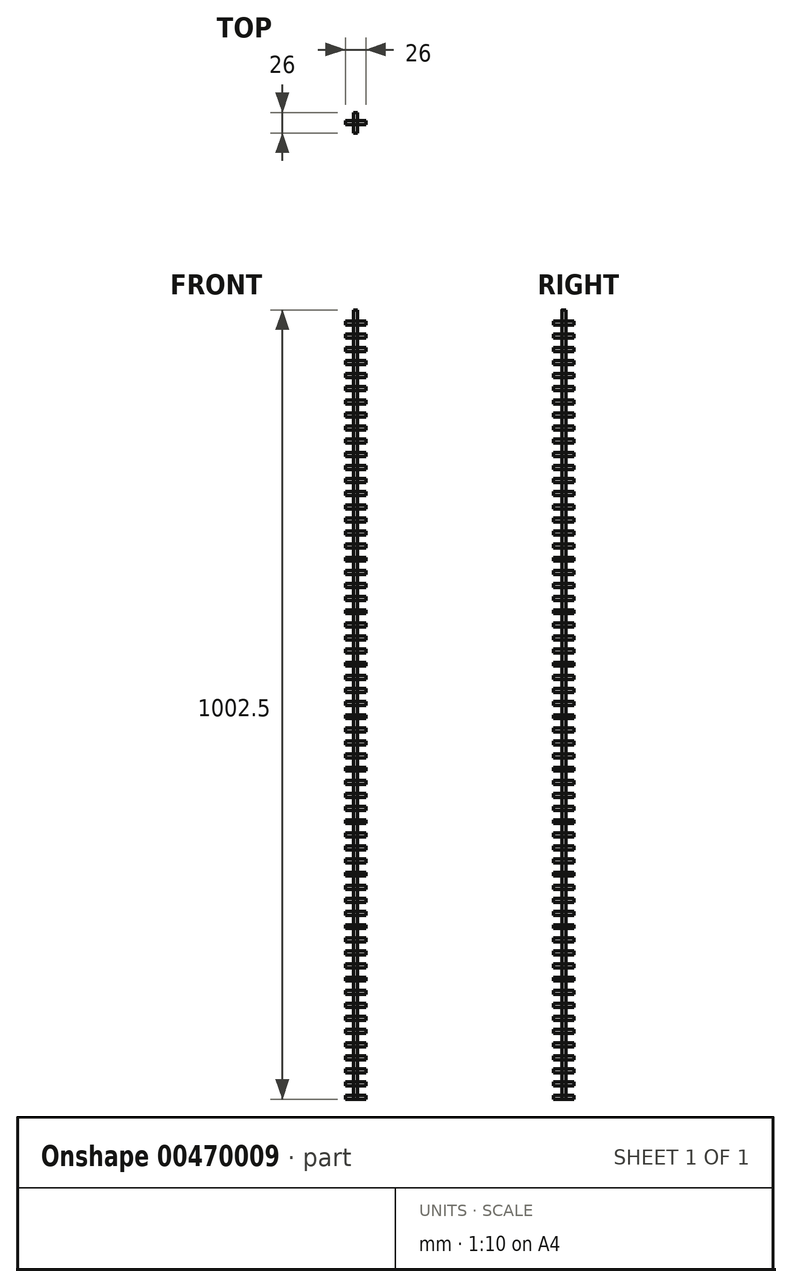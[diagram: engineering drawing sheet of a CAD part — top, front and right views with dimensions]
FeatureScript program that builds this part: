
annotation { "Feature Type Name" : "Feature", "Feature Type Description" : "" }
export const myFeature = defineFeature(function(context is Context, id is Id, definition is map)
    precondition{}
    {
        {
            var Q0;
            Q0=qCreatedBy(makeId("Top.planeOp"),FACE);
            var sketch = newSketch(context, id + "F0", { "sketchPlane" : qUnion([Q0])});
            skCircle(sketch, "E0", {"center": v(0, 0) * mm, "radius": 2.5 * mm});
            skSolve(sketch);
        }
        {
            var Q0;
            Q0 = qSketchRegion(id + "F0", true);
            extrude(context, id + "F1", {"entities" : qUnion([Q0]), "depth" : 1000 * mm, "offsetDistance" : 25 * mm});
        }
        {
            var Q0;
            Q0=qCreatedBy(makeId("Front.planeOp"),FACE);
            var sketch = newSketch(context, id + "F2", { "sketchPlane" : qUnion([Q0])});
            skLineSegment(sketch, "E1.bottom", {"start": v(2.5, 2.5) * mm, "end": v(-2.5, 2.5) * mm});
            skLineSegment(sketch, "E1.top", {"start": v(2.5, -2.5) * mm, "end": v(-2.5, -2.5) * mm});
            skLineSegment(sketch, "E1.left", {"start": v(2.5, 2.5) * mm, "end": v(2.5, -2.5) * mm});
            skLineSegment(sketch, "E1.right", {"start": v(-2.5, 2.5) * mm, "end": v(-2.5, -2.5) * mm});
            skPoint(sketch, "E1.middle", {"position": v(0, 0) * mm});
            skLineSegment(sketch, "E2.0.1.0", {"start": v(2.5, 19.17) * mm, "end": v(-2.5, 19.17) * mm});
            skLineSegment(sketch, "E2.0.1.1", {"start": v(2.5, 19.17) * mm, "end": v(2.5, 14.17) * mm});
            skLineSegment(sketch, "E2.0.1.2", {"start": v(2.5, 14.17) * mm, "end": v(-2.5, 14.17) * mm});
            skLineSegment(sketch, "E2.0.1.3", {"start": v(-2.5, 19.17) * mm, "end": v(-2.5, 14.17) * mm});
            skLineSegment(sketch, "E2.0.2.0", {"start": v(2.5, 35.83) * mm, "end": v(-2.5, 35.83) * mm});
            skLineSegment(sketch, "E2.0.2.1", {"start": v(2.5, 35.83) * mm, "end": v(2.5, 30.83) * mm});
            skLineSegment(sketch, "E2.0.2.2", {"start": v(2.5, 30.83) * mm, "end": v(-2.5, 30.83) * mm});
            skLineSegment(sketch, "E2.0.2.3", {"start": v(-2.5, 35.83) * mm, "end": v(-2.5, 30.83) * mm});
            skLineSegment(sketch, "E2.0.3.0", {"start": v(2.5, 52.5) * mm, "end": v(-2.5, 52.5) * mm});
            skLineSegment(sketch, "E2.0.3.1", {"start": v(2.5, 52.5) * mm, "end": v(2.5, 47.5) * mm});
            skLineSegment(sketch, "E2.0.3.2", {"start": v(2.5, 47.5) * mm, "end": v(-2.5, 47.5) * mm});
            skLineSegment(sketch, "E2.0.3.3", {"start": v(-2.5, 52.5) * mm, "end": v(-2.5, 47.5) * mm});
            skLineSegment(sketch, "E2.0.4.0", {"start": v(2.5, 69.17) * mm, "end": v(-2.5, 69.17) * mm});
            skLineSegment(sketch, "E2.0.4.1", {"start": v(2.5, 69.17) * mm, "end": v(2.5, 64.17) * mm});
            skLineSegment(sketch, "E2.0.4.2", {"start": v(2.5, 64.17) * mm, "end": v(-2.5, 64.17) * mm});
            skLineSegment(sketch, "E2.0.4.3", {"start": v(-2.5, 69.17) * mm, "end": v(-2.5, 64.17) * mm});
            skLineSegment(sketch, "E2.0.5.0", {"start": v(2.5, 85.83) * mm, "end": v(-2.5, 85.83) * mm});
            skLineSegment(sketch, "E2.0.5.1", {"start": v(2.5, 85.83) * mm, "end": v(2.5, 80.83) * mm});
            skLineSegment(sketch, "E2.0.5.2", {"start": v(2.5, 80.83) * mm, "end": v(-2.5, 80.83) * mm});
            skLineSegment(sketch, "E2.0.5.3", {"start": v(-2.5, 85.83) * mm, "end": v(-2.5, 80.83) * mm});
            skLineSegment(sketch, "E2.0.6.0", {"start": v(2.5, 102.5) * mm, "end": v(-2.5, 102.5) * mm});
            skLineSegment(sketch, "E2.0.6.1", {"start": v(2.5, 102.5) * mm, "end": v(2.5, 97.5) * mm});
            skLineSegment(sketch, "E2.0.6.2", {"start": v(2.5, 97.5) * mm, "end": v(-2.5, 97.5) * mm});
            skLineSegment(sketch, "E2.0.6.3", {"start": v(-2.5, 102.5) * mm, "end": v(-2.5, 97.5) * mm});
            skLineSegment(sketch, "E2.0.7.0", {"start": v(2.5, 119.17) * mm, "end": v(-2.5, 119.17) * mm});
            skLineSegment(sketch, "E2.0.7.1", {"start": v(2.5, 119.17) * mm, "end": v(2.5, 114.17) * mm});
            skLineSegment(sketch, "E2.0.7.2", {"start": v(2.5, 114.17) * mm, "end": v(-2.5, 114.17) * mm});
            skLineSegment(sketch, "E2.0.7.3", {"start": v(-2.5, 119.17) * mm, "end": v(-2.5, 114.17) * mm});
            skLineSegment(sketch, "E2.0.8.0", {"start": v(2.5, 135.83) * mm, "end": v(-2.5, 135.83) * mm});
            skLineSegment(sketch, "E2.0.8.1", {"start": v(2.5, 135.83) * mm, "end": v(2.5, 130.83) * mm});
            skLineSegment(sketch, "E2.0.8.2", {"start": v(2.5, 130.83) * mm, "end": v(-2.5, 130.83) * mm});
            skLineSegment(sketch, "E2.0.8.3", {"start": v(-2.5, 135.83) * mm, "end": v(-2.5, 130.83) * mm});
            skLineSegment(sketch, "E2.0.9.0", {"start": v(2.5, 152.5) * mm, "end": v(-2.5, 152.5) * mm});
            skLineSegment(sketch, "E2.0.9.1", {"start": v(2.5, 152.5) * mm, "end": v(2.5, 147.5) * mm});
            skLineSegment(sketch, "E2.0.9.2", {"start": v(2.5, 147.5) * mm, "end": v(-2.5, 147.5) * mm});
            skLineSegment(sketch, "E2.0.9.3", {"start": v(-2.5, 152.5) * mm, "end": v(-2.5, 147.5) * mm});
            skLineSegment(sketch, "E2.0.10.0", {"start": v(2.5, 169.17) * mm, "end": v(-2.5, 169.17) * mm});
            skLineSegment(sketch, "E2.0.10.1", {"start": v(2.5, 169.17) * mm, "end": v(2.5, 164.17) * mm});
            skLineSegment(sketch, "E2.0.10.2", {"start": v(2.5, 164.17) * mm, "end": v(-2.5, 164.17) * mm});
            skLineSegment(sketch, "E2.0.10.3", {"start": v(-2.5, 169.17) * mm, "end": v(-2.5, 164.17) * mm});
            skLineSegment(sketch, "E2.0.11.0", {"start": v(2.5, 185.83) * mm, "end": v(-2.5, 185.83) * mm});
            skLineSegment(sketch, "E2.0.11.1", {"start": v(2.5, 185.83) * mm, "end": v(2.5, 180.83) * mm});
            skLineSegment(sketch, "E2.0.11.2", {"start": v(2.5, 180.83) * mm, "end": v(-2.5, 180.83) * mm});
            skLineSegment(sketch, "E2.0.11.3", {"start": v(-2.5, 185.83) * mm, "end": v(-2.5, 180.83) * mm});
            skLineSegment(sketch, "E2.0.12.0", {"start": v(2.5, 202.5) * mm, "end": v(-2.5, 202.5) * mm});
            skLineSegment(sketch, "E2.0.12.1", {"start": v(2.5, 202.5) * mm, "end": v(2.5, 197.5) * mm});
            skLineSegment(sketch, "E2.0.12.2", {"start": v(2.5, 197.5) * mm, "end": v(-2.5, 197.5) * mm});
            skLineSegment(sketch, "E2.0.12.3", {"start": v(-2.5, 202.5) * mm, "end": v(-2.5, 197.5) * mm});
            skLineSegment(sketch, "E2.0.13.0", {"start": v(2.5, 219.17) * mm, "end": v(-2.5, 219.17) * mm});
            skLineSegment(sketch, "E2.0.13.1", {"start": v(2.5, 219.17) * mm, "end": v(2.5, 214.17) * mm});
            skLineSegment(sketch, "E2.0.13.2", {"start": v(2.5, 214.17) * mm, "end": v(-2.5, 214.17) * mm});
            skLineSegment(sketch, "E2.0.13.3", {"start": v(-2.5, 219.17) * mm, "end": v(-2.5, 214.17) * mm});
            skLineSegment(sketch, "E2.0.14.0", {"start": v(2.5, 235.83) * mm, "end": v(-2.5, 235.83) * mm});
            skLineSegment(sketch, "E2.0.14.1", {"start": v(2.5, 235.83) * mm, "end": v(2.5, 230.83) * mm});
            skLineSegment(sketch, "E2.0.14.2", {"start": v(2.5, 230.83) * mm, "end": v(-2.5, 230.83) * mm});
            skLineSegment(sketch, "E2.0.14.3", {"start": v(-2.5, 235.83) * mm, "end": v(-2.5, 230.83) * mm});
            skLineSegment(sketch, "E2.0.15.0", {"start": v(2.5, 252.5) * mm, "end": v(-2.5, 252.5) * mm});
            skLineSegment(sketch, "E2.0.15.1", {"start": v(2.5, 252.5) * mm, "end": v(2.5, 247.5) * mm});
            skLineSegment(sketch, "E2.0.15.2", {"start": v(2.5, 247.5) * mm, "end": v(-2.5, 247.5) * mm});
            skLineSegment(sketch, "E2.0.15.3", {"start": v(-2.5, 252.5) * mm, "end": v(-2.5, 247.5) * mm});
            skLineSegment(sketch, "E2.0.16.0", {"start": v(2.5, 269.17) * mm, "end": v(-2.5, 269.17) * mm});
            skLineSegment(sketch, "E2.0.16.1", {"start": v(2.5, 269.17) * mm, "end": v(2.5, 264.17) * mm});
            skLineSegment(sketch, "E2.0.16.2", {"start": v(2.5, 264.17) * mm, "end": v(-2.5, 264.17) * mm});
            skLineSegment(sketch, "E2.0.16.3", {"start": v(-2.5, 269.17) * mm, "end": v(-2.5, 264.17) * mm});
            skLineSegment(sketch, "E2.0.17.0", {"start": v(2.5, 285.83) * mm, "end": v(-2.5, 285.83) * mm});
            skLineSegment(sketch, "E2.0.17.1", {"start": v(2.5, 285.83) * mm, "end": v(2.5, 280.83) * mm});
            skLineSegment(sketch, "E2.0.17.2", {"start": v(2.5, 280.83) * mm, "end": v(-2.5, 280.83) * mm});
            skLineSegment(sketch, "E2.0.17.3", {"start": v(-2.5, 285.83) * mm, "end": v(-2.5, 280.83) * mm});
            skLineSegment(sketch, "E2.0.18.0", {"start": v(2.5, 302.5) * mm, "end": v(-2.5, 302.5) * mm});
            skLineSegment(sketch, "E2.0.18.1", {"start": v(2.5, 302.5) * mm, "end": v(2.5, 297.5) * mm});
            skLineSegment(sketch, "E2.0.18.2", {"start": v(2.5, 297.5) * mm, "end": v(-2.5, 297.5) * mm});
            skLineSegment(sketch, "E2.0.18.3", {"start": v(-2.5, 302.5) * mm, "end": v(-2.5, 297.5) * mm});
            skLineSegment(sketch, "E2.0.19.0", {"start": v(2.5, 319.17) * mm, "end": v(-2.5, 319.17) * mm});
            skLineSegment(sketch, "E2.0.19.1", {"start": v(2.5, 319.17) * mm, "end": v(2.5, 314.17) * mm});
            skLineSegment(sketch, "E2.0.19.2", {"start": v(2.5, 314.17) * mm, "end": v(-2.5, 314.17) * mm});
            skLineSegment(sketch, "E2.0.19.3", {"start": v(-2.5, 319.17) * mm, "end": v(-2.5, 314.17) * mm});
            skLineSegment(sketch, "E2.0.20.0", {"start": v(2.5, 335.83) * mm, "end": v(-2.5, 335.83) * mm});
            skLineSegment(sketch, "E2.0.20.1", {"start": v(2.5, 335.83) * mm, "end": v(2.5, 330.83) * mm});
            skLineSegment(sketch, "E2.0.20.2", {"start": v(2.5, 330.83) * mm, "end": v(-2.5, 330.83) * mm});
            skLineSegment(sketch, "E2.0.20.3", {"start": v(-2.5, 335.83) * mm, "end": v(-2.5, 330.83) * mm});
            skLineSegment(sketch, "E2.0.21.0", {"start": v(2.5, 352.5) * mm, "end": v(-2.5, 352.5) * mm});
            skLineSegment(sketch, "E2.0.21.1", {"start": v(2.5, 352.5) * mm, "end": v(2.5, 347.5) * mm});
            skLineSegment(sketch, "E2.0.21.2", {"start": v(2.5, 347.5) * mm, "end": v(-2.5, 347.5) * mm});
            skLineSegment(sketch, "E2.0.21.3", {"start": v(-2.5, 352.5) * mm, "end": v(-2.5, 347.5) * mm});
            skLineSegment(sketch, "E2.0.22.0", {"start": v(2.5, 369.17) * mm, "end": v(-2.5, 369.17) * mm});
            skLineSegment(sketch, "E2.0.22.1", {"start": v(2.5, 369.17) * mm, "end": v(2.5, 364.17) * mm});
            skLineSegment(sketch, "E2.0.22.2", {"start": v(2.5, 364.17) * mm, "end": v(-2.5, 364.17) * mm});
            skLineSegment(sketch, "E2.0.22.3", {"start": v(-2.5, 369.17) * mm, "end": v(-2.5, 364.17) * mm});
            skLineSegment(sketch, "E2.0.23.0", {"start": v(2.5, 385.83) * mm, "end": v(-2.5, 385.83) * mm});
            skLineSegment(sketch, "E2.0.23.1", {"start": v(2.5, 385.83) * mm, "end": v(2.5, 380.83) * mm});
            skLineSegment(sketch, "E2.0.23.2", {"start": v(2.5, 380.83) * mm, "end": v(-2.5, 380.83) * mm});
            skLineSegment(sketch, "E2.0.23.3", {"start": v(-2.5, 385.83) * mm, "end": v(-2.5, 380.83) * mm});
            skLineSegment(sketch, "E2.0.24.0", {"start": v(2.5, 402.5) * mm, "end": v(-2.5, 402.5) * mm});
            skLineSegment(sketch, "E2.0.24.1", {"start": v(2.5, 402.5) * mm, "end": v(2.5, 397.5) * mm});
            skLineSegment(sketch, "E2.0.24.2", {"start": v(2.5, 397.5) * mm, "end": v(-2.5, 397.5) * mm});
            skLineSegment(sketch, "E2.0.24.3", {"start": v(-2.5, 402.5) * mm, "end": v(-2.5, 397.5) * mm});
            skLineSegment(sketch, "E2.0.25.0", {"start": v(2.5, 419.17) * mm, "end": v(-2.5, 419.17) * mm});
            skLineSegment(sketch, "E2.0.25.1", {"start": v(2.5, 419.17) * mm, "end": v(2.5, 414.17) * mm});
            skLineSegment(sketch, "E2.0.25.2", {"start": v(2.5, 414.17) * mm, "end": v(-2.5, 414.17) * mm});
            skLineSegment(sketch, "E2.0.25.3", {"start": v(-2.5, 419.17) * mm, "end": v(-2.5, 414.17) * mm});
            skLineSegment(sketch, "E2.0.26.0", {"start": v(2.5, 435.83) * mm, "end": v(-2.5, 435.83) * mm});
            skLineSegment(sketch, "E2.0.26.1", {"start": v(2.5, 435.83) * mm, "end": v(2.5, 430.83) * mm});
            skLineSegment(sketch, "E2.0.26.2", {"start": v(2.5, 430.83) * mm, "end": v(-2.5, 430.83) * mm});
            skLineSegment(sketch, "E2.0.26.3", {"start": v(-2.5, 435.83) * mm, "end": v(-2.5, 430.83) * mm});
            skLineSegment(sketch, "E2.0.27.0", {"start": v(2.5, 452.5) * mm, "end": v(-2.5, 452.5) * mm});
            skLineSegment(sketch, "E2.0.27.1", {"start": v(2.5, 452.5) * mm, "end": v(2.5, 447.5) * mm});
            skLineSegment(sketch, "E2.0.27.2", {"start": v(2.5, 447.5) * mm, "end": v(-2.5, 447.5) * mm});
            skLineSegment(sketch, "E2.0.27.3", {"start": v(-2.5, 452.5) * mm, "end": v(-2.5, 447.5) * mm});
            skLineSegment(sketch, "E2.0.28.0", {"start": v(2.5, 469.17) * mm, "end": v(-2.5, 469.17) * mm});
            skLineSegment(sketch, "E2.0.28.1", {"start": v(2.5, 469.17) * mm, "end": v(2.5, 464.17) * mm});
            skLineSegment(sketch, "E2.0.28.2", {"start": v(2.5, 464.17) * mm, "end": v(-2.5, 464.17) * mm});
            skLineSegment(sketch, "E2.0.28.3", {"start": v(-2.5, 469.17) * mm, "end": v(-2.5, 464.17) * mm});
            skLineSegment(sketch, "E2.0.29.0", {"start": v(2.5, 485.83) * mm, "end": v(-2.5, 485.83) * mm});
            skLineSegment(sketch, "E2.0.29.1", {"start": v(2.5, 485.83) * mm, "end": v(2.5, 480.83) * mm});
            skLineSegment(sketch, "E2.0.29.2", {"start": v(2.5, 480.83) * mm, "end": v(-2.5, 480.83) * mm});
            skLineSegment(sketch, "E2.0.29.3", {"start": v(-2.5, 485.83) * mm, "end": v(-2.5, 480.83) * mm});
            skLineSegment(sketch, "E2.0.30.0", {"start": v(2.5, 502.5) * mm, "end": v(-2.5, 502.5) * mm});
            skLineSegment(sketch, "E2.0.30.1", {"start": v(2.5, 502.5) * mm, "end": v(2.5, 497.5) * mm});
            skLineSegment(sketch, "E2.0.30.2", {"start": v(2.5, 497.5) * mm, "end": v(-2.5, 497.5) * mm});
            skLineSegment(sketch, "E2.0.30.3", {"start": v(-2.5, 502.5) * mm, "end": v(-2.5, 497.5) * mm});
            skLineSegment(sketch, "E2.0.31.0", {"start": v(2.5, 519.17) * mm, "end": v(-2.5, 519.17) * mm});
            skLineSegment(sketch, "E2.0.31.1", {"start": v(2.5, 519.17) * mm, "end": v(2.5, 514.17) * mm});
            skLineSegment(sketch, "E2.0.31.2", {"start": v(2.5, 514.17) * mm, "end": v(-2.5, 514.17) * mm});
            skLineSegment(sketch, "E2.0.31.3", {"start": v(-2.5, 519.17) * mm, "end": v(-2.5, 514.17) * mm});
            skLineSegment(sketch, "E2.0.32.0", {"start": v(2.5, 535.83) * mm, "end": v(-2.5, 535.83) * mm});
            skLineSegment(sketch, "E2.0.32.1", {"start": v(2.5, 535.83) * mm, "end": v(2.5, 530.83) * mm});
            skLineSegment(sketch, "E2.0.32.2", {"start": v(2.5, 530.83) * mm, "end": v(-2.5, 530.83) * mm});
            skLineSegment(sketch, "E2.0.32.3", {"start": v(-2.5, 535.83) * mm, "end": v(-2.5, 530.83) * mm});
            skLineSegment(sketch, "E2.0.33.0", {"start": v(2.5, 552.5) * mm, "end": v(-2.5, 552.5) * mm});
            skLineSegment(sketch, "E2.0.33.1", {"start": v(2.5, 552.5) * mm, "end": v(2.5, 547.5) * mm});
            skLineSegment(sketch, "E2.0.33.2", {"start": v(2.5, 547.5) * mm, "end": v(-2.5, 547.5) * mm});
            skLineSegment(sketch, "E2.0.33.3", {"start": v(-2.5, 552.5) * mm, "end": v(-2.5, 547.5) * mm});
            skLineSegment(sketch, "E2.0.34.0", {"start": v(2.5, 569.17) * mm, "end": v(-2.5, 569.17) * mm});
            skLineSegment(sketch, "E2.0.34.1", {"start": v(2.5, 569.17) * mm, "end": v(2.5, 564.17) * mm});
            skLineSegment(sketch, "E2.0.34.2", {"start": v(2.5, 564.17) * mm, "end": v(-2.5, 564.17) * mm});
            skLineSegment(sketch, "E2.0.34.3", {"start": v(-2.5, 569.17) * mm, "end": v(-2.5, 564.17) * mm});
            skLineSegment(sketch, "E2.0.35.0", {"start": v(2.5, 585.83) * mm, "end": v(-2.5, 585.83) * mm});
            skLineSegment(sketch, "E2.0.35.1", {"start": v(2.5, 585.83) * mm, "end": v(2.5, 580.83) * mm});
            skLineSegment(sketch, "E2.0.35.2", {"start": v(2.5, 580.83) * mm, "end": v(-2.5, 580.83) * mm});
            skLineSegment(sketch, "E2.0.35.3", {"start": v(-2.5, 585.83) * mm, "end": v(-2.5, 580.83) * mm});
            skLineSegment(sketch, "E2.0.36.0", {"start": v(2.5, 602.5) * mm, "end": v(-2.5, 602.5) * mm});
            skLineSegment(sketch, "E2.0.36.1", {"start": v(2.5, 602.5) * mm, "end": v(2.5, 597.5) * mm});
            skLineSegment(sketch, "E2.0.36.2", {"start": v(2.5, 597.5) * mm, "end": v(-2.5, 597.5) * mm});
            skLineSegment(sketch, "E2.0.36.3", {"start": v(-2.5, 602.5) * mm, "end": v(-2.5, 597.5) * mm});
            skLineSegment(sketch, "E2.0.37.0", {"start": v(2.5, 619.17) * mm, "end": v(-2.5, 619.17) * mm});
            skLineSegment(sketch, "E2.0.37.1", {"start": v(2.5, 619.17) * mm, "end": v(2.5, 614.17) * mm});
            skLineSegment(sketch, "E2.0.37.2", {"start": v(2.5, 614.17) * mm, "end": v(-2.5, 614.17) * mm});
            skLineSegment(sketch, "E2.0.37.3", {"start": v(-2.5, 619.17) * mm, "end": v(-2.5, 614.17) * mm});
            skLineSegment(sketch, "E2.0.38.0", {"start": v(2.5, 635.83) * mm, "end": v(-2.5, 635.83) * mm});
            skLineSegment(sketch, "E2.0.38.1", {"start": v(2.5, 635.83) * mm, "end": v(2.5, 630.83) * mm});
            skLineSegment(sketch, "E2.0.38.2", {"start": v(2.5, 630.83) * mm, "end": v(-2.5, 630.83) * mm});
            skLineSegment(sketch, "E2.0.38.3", {"start": v(-2.5, 635.83) * mm, "end": v(-2.5, 630.83) * mm});
            skLineSegment(sketch, "E2.0.39.0", {"start": v(2.5, 652.5) * mm, "end": v(-2.5, 652.5) * mm});
            skLineSegment(sketch, "E2.0.39.1", {"start": v(2.5, 652.5) * mm, "end": v(2.5, 647.5) * mm});
            skLineSegment(sketch, "E2.0.39.2", {"start": v(2.5, 647.5) * mm, "end": v(-2.5, 647.5) * mm});
            skLineSegment(sketch, "E2.0.39.3", {"start": v(-2.5, 652.5) * mm, "end": v(-2.5, 647.5) * mm});
            skLineSegment(sketch, "E2.0.40.0", {"start": v(2.5, 669.17) * mm, "end": v(-2.5, 669.17) * mm});
            skLineSegment(sketch, "E2.0.40.1", {"start": v(2.5, 669.17) * mm, "end": v(2.5, 664.17) * mm});
            skLineSegment(sketch, "E2.0.40.2", {"start": v(2.5, 664.17) * mm, "end": v(-2.5, 664.17) * mm});
            skLineSegment(sketch, "E2.0.40.3", {"start": v(-2.5, 669.17) * mm, "end": v(-2.5, 664.17) * mm});
            skLineSegment(sketch, "E2.0.41.0", {"start": v(2.5, 685.83) * mm, "end": v(-2.5, 685.83) * mm});
            skLineSegment(sketch, "E2.0.41.1", {"start": v(2.5, 685.83) * mm, "end": v(2.5, 680.83) * mm});
            skLineSegment(sketch, "E2.0.41.2", {"start": v(2.5, 680.83) * mm, "end": v(-2.5, 680.83) * mm});
            skLineSegment(sketch, "E2.0.41.3", {"start": v(-2.5, 685.83) * mm, "end": v(-2.5, 680.83) * mm});
            skLineSegment(sketch, "E2.0.42.0", {"start": v(2.5, 702.5) * mm, "end": v(-2.5, 702.5) * mm});
            skLineSegment(sketch, "E2.0.42.1", {"start": v(2.5, 702.5) * mm, "end": v(2.5, 697.5) * mm});
            skLineSegment(sketch, "E2.0.42.2", {"start": v(2.5, 697.5) * mm, "end": v(-2.5, 697.5) * mm});
            skLineSegment(sketch, "E2.0.42.3", {"start": v(-2.5, 702.5) * mm, "end": v(-2.5, 697.5) * mm});
            skLineSegment(sketch, "E2.0.43.0", {"start": v(2.5, 719.17) * mm, "end": v(-2.5, 719.17) * mm});
            skLineSegment(sketch, "E2.0.43.1", {"start": v(2.5, 719.17) * mm, "end": v(2.5, 714.17) * mm});
            skLineSegment(sketch, "E2.0.43.2", {"start": v(2.5, 714.17) * mm, "end": v(-2.5, 714.17) * mm});
            skLineSegment(sketch, "E2.0.43.3", {"start": v(-2.5, 719.17) * mm, "end": v(-2.5, 714.17) * mm});
            skLineSegment(sketch, "E2.0.44.0", {"start": v(2.5, 735.83) * mm, "end": v(-2.5, 735.83) * mm});
            skLineSegment(sketch, "E2.0.44.1", {"start": v(2.5, 735.83) * mm, "end": v(2.5, 730.83) * mm});
            skLineSegment(sketch, "E2.0.44.2", {"start": v(2.5, 730.83) * mm, "end": v(-2.5, 730.83) * mm});
            skLineSegment(sketch, "E2.0.44.3", {"start": v(-2.5, 735.83) * mm, "end": v(-2.5, 730.83) * mm});
            skLineSegment(sketch, "E2.0.45.0", {"start": v(2.5, 752.5) * mm, "end": v(-2.5, 752.5) * mm});
            skLineSegment(sketch, "E2.0.45.1", {"start": v(2.5, 752.5) * mm, "end": v(2.5, 747.5) * mm});
            skLineSegment(sketch, "E2.0.45.2", {"start": v(2.5, 747.5) * mm, "end": v(-2.5, 747.5) * mm});
            skLineSegment(sketch, "E2.0.45.3", {"start": v(-2.5, 752.5) * mm, "end": v(-2.5, 747.5) * mm});
            skLineSegment(sketch, "E2.0.46.0", {"start": v(2.5, 769.17) * mm, "end": v(-2.5, 769.17) * mm});
            skLineSegment(sketch, "E2.0.46.1", {"start": v(2.5, 769.17) * mm, "end": v(2.5, 764.17) * mm});
            skLineSegment(sketch, "E2.0.46.2", {"start": v(2.5, 764.17) * mm, "end": v(-2.5, 764.17) * mm});
            skLineSegment(sketch, "E2.0.46.3", {"start": v(-2.5, 769.17) * mm, "end": v(-2.5, 764.17) * mm});
            skLineSegment(sketch, "E2.0.47.0", {"start": v(2.5, 785.83) * mm, "end": v(-2.5, 785.83) * mm});
            skLineSegment(sketch, "E2.0.47.1", {"start": v(2.5, 785.83) * mm, "end": v(2.5, 780.83) * mm});
            skLineSegment(sketch, "E2.0.47.2", {"start": v(2.5, 780.83) * mm, "end": v(-2.5, 780.83) * mm});
            skLineSegment(sketch, "E2.0.47.3", {"start": v(-2.5, 785.83) * mm, "end": v(-2.5, 780.83) * mm});
            skLineSegment(sketch, "E2.0.48.0", {"start": v(2.5, 802.5) * mm, "end": v(-2.5, 802.5) * mm});
            skLineSegment(sketch, "E2.0.48.1", {"start": v(2.5, 802.5) * mm, "end": v(2.5, 797.5) * mm});
            skLineSegment(sketch, "E2.0.48.2", {"start": v(2.5, 797.5) * mm, "end": v(-2.5, 797.5) * mm});
            skLineSegment(sketch, "E2.0.48.3", {"start": v(-2.5, 802.5) * mm, "end": v(-2.5, 797.5) * mm});
            skLineSegment(sketch, "E2.0.49.0", {"start": v(2.5, 819.17) * mm, "end": v(-2.5, 819.17) * mm});
            skLineSegment(sketch, "E2.0.49.1", {"start": v(2.5, 819.17) * mm, "end": v(2.5, 814.17) * mm});
            skLineSegment(sketch, "E2.0.49.2", {"start": v(2.5, 814.17) * mm, "end": v(-2.5, 814.17) * mm});
            skLineSegment(sketch, "E2.0.49.3", {"start": v(-2.5, 819.17) * mm, "end": v(-2.5, 814.17) * mm});
            skLineSegment(sketch, "E2.0.50.0", {"start": v(2.5, 835.83) * mm, "end": v(-2.5, 835.83) * mm});
            skLineSegment(sketch, "E2.0.50.1", {"start": v(2.5, 835.83) * mm, "end": v(2.5, 830.83) * mm});
            skLineSegment(sketch, "E2.0.50.2", {"start": v(2.5, 830.83) * mm, "end": v(-2.5, 830.83) * mm});
            skLineSegment(sketch, "E2.0.50.3", {"start": v(-2.5, 835.83) * mm, "end": v(-2.5, 830.83) * mm});
            skLineSegment(sketch, "E2.0.51.0", {"start": v(2.5, 852.5) * mm, "end": v(-2.5, 852.5) * mm});
            skLineSegment(sketch, "E2.0.51.1", {"start": v(2.5, 852.5) * mm, "end": v(2.5, 847.5) * mm});
            skLineSegment(sketch, "E2.0.51.2", {"start": v(2.5, 847.5) * mm, "end": v(-2.5, 847.5) * mm});
            skLineSegment(sketch, "E2.0.51.3", {"start": v(-2.5, 852.5) * mm, "end": v(-2.5, 847.5) * mm});
            skLineSegment(sketch, "E2.0.52.0", {"start": v(2.5, 869.17) * mm, "end": v(-2.5, 869.17) * mm});
            skLineSegment(sketch, "E2.0.52.1", {"start": v(2.5, 869.17) * mm, "end": v(2.5, 864.17) * mm});
            skLineSegment(sketch, "E2.0.52.2", {"start": v(2.5, 864.17) * mm, "end": v(-2.5, 864.17) * mm});
            skLineSegment(sketch, "E2.0.52.3", {"start": v(-2.5, 869.17) * mm, "end": v(-2.5, 864.17) * mm});
            skLineSegment(sketch, "E2.0.53.0", {"start": v(2.5, 885.83) * mm, "end": v(-2.5, 885.83) * mm});
            skLineSegment(sketch, "E2.0.53.1", {"start": v(2.5, 885.83) * mm, "end": v(2.5, 880.83) * mm});
            skLineSegment(sketch, "E2.0.53.2", {"start": v(2.5, 880.83) * mm, "end": v(-2.5, 880.83) * mm});
            skLineSegment(sketch, "E2.0.53.3", {"start": v(-2.5, 885.83) * mm, "end": v(-2.5, 880.83) * mm});
            skLineSegment(sketch, "E2.0.54.0", {"start": v(2.5, 902.5) * mm, "end": v(-2.5, 902.5) * mm});
            skLineSegment(sketch, "E2.0.54.1", {"start": v(2.5, 902.5) * mm, "end": v(2.5, 897.5) * mm});
            skLineSegment(sketch, "E2.0.54.2", {"start": v(2.5, 897.5) * mm, "end": v(-2.5, 897.5) * mm});
            skLineSegment(sketch, "E2.0.54.3", {"start": v(-2.5, 902.5) * mm, "end": v(-2.5, 897.5) * mm});
            skLineSegment(sketch, "E2.0.55.0", {"start": v(2.5, 919.17) * mm, "end": v(-2.5, 919.17) * mm});
            skLineSegment(sketch, "E2.0.55.1", {"start": v(2.5, 919.17) * mm, "end": v(2.5, 914.17) * mm});
            skLineSegment(sketch, "E2.0.55.2", {"start": v(2.5, 914.17) * mm, "end": v(-2.5, 914.17) * mm});
            skLineSegment(sketch, "E2.0.55.3", {"start": v(-2.5, 919.17) * mm, "end": v(-2.5, 914.17) * mm});
            skLineSegment(sketch, "E2.0.56.0", {"start": v(2.5, 935.83) * mm, "end": v(-2.5, 935.83) * mm});
            skLineSegment(sketch, "E2.0.56.1", {"start": v(2.5, 935.83) * mm, "end": v(2.5, 930.83) * mm});
            skLineSegment(sketch, "E2.0.56.2", {"start": v(2.5, 930.83) * mm, "end": v(-2.5, 930.83) * mm});
            skLineSegment(sketch, "E2.0.56.3", {"start": v(-2.5, 935.83) * mm, "end": v(-2.5, 930.83) * mm});
            skLineSegment(sketch, "E2.0.57.0", {"start": v(2.5, 952.5) * mm, "end": v(-2.5, 952.5) * mm});
            skLineSegment(sketch, "E2.0.57.1", {"start": v(2.5, 952.5) * mm, "end": v(2.5, 947.5) * mm});
            skLineSegment(sketch, "E2.0.57.2", {"start": v(2.5, 947.5) * mm, "end": v(-2.5, 947.5) * mm});
            skLineSegment(sketch, "E2.0.57.3", {"start": v(-2.5, 952.5) * mm, "end": v(-2.5, 947.5) * mm});
            skLineSegment(sketch, "E2.0.58.0", {"start": v(2.5, 969.17) * mm, "end": v(-2.5, 969.17) * mm});
            skLineSegment(sketch, "E2.0.58.1", {"start": v(2.5, 969.17) * mm, "end": v(2.5, 964.17) * mm});
            skLineSegment(sketch, "E2.0.58.2", {"start": v(2.5, 964.17) * mm, "end": v(-2.5, 964.17) * mm});
            skLineSegment(sketch, "E2.0.58.3", {"start": v(-2.5, 969.17) * mm, "end": v(-2.5, 964.17) * mm});
            skLineSegment(sketch, "E2.0.59.0", {"start": v(2.5, 985.83) * mm, "end": v(-2.5, 985.83) * mm});
            skLineSegment(sketch, "E2.0.59.1", {"start": v(2.5, 985.83) * mm, "end": v(2.5, 980.83) * mm});
            skLineSegment(sketch, "E2.0.59.2", {"start": v(2.5, 980.83) * mm, "end": v(-2.5, 980.83) * mm});
            skLineSegment(sketch, "E2.0.59.3", {"start": v(-2.5, 985.83) * mm, "end": v(-2.5, 980.83) * mm});
            skLineSegment(sketch, "E2.direction1", {"start": v(-2.5, 2.5) * mm, "end": v(22.5, 2.5) * mm, "construction": true});
            skLineSegment(sketch, "E2.direction2", {"start": v(-2.5, 2.5) * mm, "end": v(-2.5, 19.17) * mm, "construction": true});
            skSolve(sketch);
        }
        {
            var Q0;
            Q0=qCreatedBy(makeId("Right.planeOp"),FACE);
            var sketch = newSketch(context, id + "F3", { "sketchPlane" : qUnion([Q0])});
            skLineSegment(sketch, "E3.bottom", {"start": v(2.5, 2.5) * mm, "end": v(-2.5, 2.5) * mm});
            skLineSegment(sketch, "E3.top", {"start": v(2.5, -2.5) * mm, "end": v(-2.5, -2.5) * mm});
            skLineSegment(sketch, "E3.left", {"start": v(2.5, 2.5) * mm, "end": v(2.5, -2.5) * mm});
            skLineSegment(sketch, "E3.right", {"start": v(-2.5, 2.5) * mm, "end": v(-2.5, -2.5) * mm});
            skPoint(sketch, "E3.middle", {"position": v(0, 0) * mm});
            skLineSegment(sketch, "E4.0.1.0", {"start": v(2.5, 19.17) * mm, "end": v(-2.5, 19.17) * mm});
            skLineSegment(sketch, "E4.0.1.1", {"start": v(2.5, 19.17) * mm, "end": v(2.5, 14.17) * mm});
            skLineSegment(sketch, "E4.0.1.2", {"start": v(2.5, 14.17) * mm, "end": v(-2.5, 14.17) * mm});
            skLineSegment(sketch, "E4.0.1.3", {"start": v(-2.5, 19.17) * mm, "end": v(-2.5, 14.17) * mm});
            skLineSegment(sketch, "E4.0.2.0", {"start": v(2.5, 35.83) * mm, "end": v(-2.5, 35.83) * mm});
            skLineSegment(sketch, "E4.0.2.1", {"start": v(2.5, 35.83) * mm, "end": v(2.5, 30.83) * mm});
            skLineSegment(sketch, "E4.0.2.2", {"start": v(2.5, 30.83) * mm, "end": v(-2.5, 30.83) * mm});
            skLineSegment(sketch, "E4.0.2.3", {"start": v(-2.5, 35.83) * mm, "end": v(-2.5, 30.83) * mm});
            skLineSegment(sketch, "E4.0.3.0", {"start": v(2.5, 52.5) * mm, "end": v(-2.5, 52.5) * mm});
            skLineSegment(sketch, "E4.0.3.1", {"start": v(2.5, 52.5) * mm, "end": v(2.5, 47.5) * mm});
            skLineSegment(sketch, "E4.0.3.2", {"start": v(2.5, 47.5) * mm, "end": v(-2.5, 47.5) * mm});
            skLineSegment(sketch, "E4.0.3.3", {"start": v(-2.5, 52.5) * mm, "end": v(-2.5, 47.5) * mm});
            skLineSegment(sketch, "E4.0.4.0", {"start": v(2.5, 69.17) * mm, "end": v(-2.5, 69.17) * mm});
            skLineSegment(sketch, "E4.0.4.1", {"start": v(2.5, 69.17) * mm, "end": v(2.5, 64.17) * mm});
            skLineSegment(sketch, "E4.0.4.2", {"start": v(2.5, 64.17) * mm, "end": v(-2.5, 64.17) * mm});
            skLineSegment(sketch, "E4.0.4.3", {"start": v(-2.5, 69.17) * mm, "end": v(-2.5, 64.17) * mm});
            skLineSegment(sketch, "E4.0.5.0", {"start": v(2.5, 85.83) * mm, "end": v(-2.5, 85.83) * mm});
            skLineSegment(sketch, "E4.0.5.1", {"start": v(2.5, 85.83) * mm, "end": v(2.5, 80.83) * mm});
            skLineSegment(sketch, "E4.0.5.2", {"start": v(2.5, 80.83) * mm, "end": v(-2.5, 80.83) * mm});
            skLineSegment(sketch, "E4.0.5.3", {"start": v(-2.5, 85.83) * mm, "end": v(-2.5, 80.83) * mm});
            skLineSegment(sketch, "E4.0.6.0", {"start": v(2.5, 102.5) * mm, "end": v(-2.5, 102.5) * mm});
            skLineSegment(sketch, "E4.0.6.1", {"start": v(2.5, 102.5) * mm, "end": v(2.5, 97.5) * mm});
            skLineSegment(sketch, "E4.0.6.2", {"start": v(2.5, 97.5) * mm, "end": v(-2.5, 97.5) * mm});
            skLineSegment(sketch, "E4.0.6.3", {"start": v(-2.5, 102.5) * mm, "end": v(-2.5, 97.5) * mm});
            skLineSegment(sketch, "E4.0.7.0", {"start": v(2.5, 119.17) * mm, "end": v(-2.5, 119.17) * mm});
            skLineSegment(sketch, "E4.0.7.1", {"start": v(2.5, 119.17) * mm, "end": v(2.5, 114.17) * mm});
            skLineSegment(sketch, "E4.0.7.2", {"start": v(2.5, 114.17) * mm, "end": v(-2.5, 114.17) * mm});
            skLineSegment(sketch, "E4.0.7.3", {"start": v(-2.5, 119.17) * mm, "end": v(-2.5, 114.17) * mm});
            skLineSegment(sketch, "E4.0.8.0", {"start": v(2.5, 135.83) * mm, "end": v(-2.5, 135.83) * mm});
            skLineSegment(sketch, "E4.0.8.1", {"start": v(2.5, 135.83) * mm, "end": v(2.5, 130.83) * mm});
            skLineSegment(sketch, "E4.0.8.2", {"start": v(2.5, 130.83) * mm, "end": v(-2.5, 130.83) * mm});
            skLineSegment(sketch, "E4.0.8.3", {"start": v(-2.5, 135.83) * mm, "end": v(-2.5, 130.83) * mm});
            skLineSegment(sketch, "E4.0.9.0", {"start": v(2.5, 152.5) * mm, "end": v(-2.5, 152.5) * mm});
            skLineSegment(sketch, "E4.0.9.1", {"start": v(2.5, 152.5) * mm, "end": v(2.5, 147.5) * mm});
            skLineSegment(sketch, "E4.0.9.2", {"start": v(2.5, 147.5) * mm, "end": v(-2.5, 147.5) * mm});
            skLineSegment(sketch, "E4.0.9.3", {"start": v(-2.5, 152.5) * mm, "end": v(-2.5, 147.5) * mm});
            skLineSegment(sketch, "E4.0.10.0", {"start": v(2.5, 169.17) * mm, "end": v(-2.5, 169.17) * mm});
            skLineSegment(sketch, "E4.0.10.1", {"start": v(2.5, 169.17) * mm, "end": v(2.5, 164.17) * mm});
            skLineSegment(sketch, "E4.0.10.2", {"start": v(2.5, 164.17) * mm, "end": v(-2.5, 164.17) * mm});
            skLineSegment(sketch, "E4.0.10.3", {"start": v(-2.5, 169.17) * mm, "end": v(-2.5, 164.17) * mm});
            skLineSegment(sketch, "E4.0.11.0", {"start": v(2.5, 185.83) * mm, "end": v(-2.5, 185.83) * mm});
            skLineSegment(sketch, "E4.0.11.1", {"start": v(2.5, 185.83) * mm, "end": v(2.5, 180.83) * mm});
            skLineSegment(sketch, "E4.0.11.2", {"start": v(2.5, 180.83) * mm, "end": v(-2.5, 180.83) * mm});
            skLineSegment(sketch, "E4.0.11.3", {"start": v(-2.5, 185.83) * mm, "end": v(-2.5, 180.83) * mm});
            skLineSegment(sketch, "E4.0.12.0", {"start": v(2.5, 202.5) * mm, "end": v(-2.5, 202.5) * mm});
            skLineSegment(sketch, "E4.0.12.1", {"start": v(2.5, 202.5) * mm, "end": v(2.5, 197.5) * mm});
            skLineSegment(sketch, "E4.0.12.2", {"start": v(2.5, 197.5) * mm, "end": v(-2.5, 197.5) * mm});
            skLineSegment(sketch, "E4.0.12.3", {"start": v(-2.5, 202.5) * mm, "end": v(-2.5, 197.5) * mm});
            skLineSegment(sketch, "E4.0.13.0", {"start": v(2.5, 219.17) * mm, "end": v(-2.5, 219.17) * mm});
            skLineSegment(sketch, "E4.0.13.1", {"start": v(2.5, 219.17) * mm, "end": v(2.5, 214.17) * mm});
            skLineSegment(sketch, "E4.0.13.2", {"start": v(2.5, 214.17) * mm, "end": v(-2.5, 214.17) * mm});
            skLineSegment(sketch, "E4.0.13.3", {"start": v(-2.5, 219.17) * mm, "end": v(-2.5, 214.17) * mm});
            skLineSegment(sketch, "E4.0.14.0", {"start": v(2.5, 235.83) * mm, "end": v(-2.5, 235.83) * mm});
            skLineSegment(sketch, "E4.0.14.1", {"start": v(2.5, 235.83) * mm, "end": v(2.5, 230.83) * mm});
            skLineSegment(sketch, "E4.0.14.2", {"start": v(2.5, 230.83) * mm, "end": v(-2.5, 230.83) * mm});
            skLineSegment(sketch, "E4.0.14.3", {"start": v(-2.5, 235.83) * mm, "end": v(-2.5, 230.83) * mm});
            skLineSegment(sketch, "E4.0.15.0", {"start": v(2.5, 252.5) * mm, "end": v(-2.5, 252.5) * mm});
            skLineSegment(sketch, "E4.0.15.1", {"start": v(2.5, 252.5) * mm, "end": v(2.5, 247.5) * mm});
            skLineSegment(sketch, "E4.0.15.2", {"start": v(2.5, 247.5) * mm, "end": v(-2.5, 247.5) * mm});
            skLineSegment(sketch, "E4.0.15.3", {"start": v(-2.5, 252.5) * mm, "end": v(-2.5, 247.5) * mm});
            skLineSegment(sketch, "E4.0.16.0", {"start": v(2.5, 269.17) * mm, "end": v(-2.5, 269.17) * mm});
            skLineSegment(sketch, "E4.0.16.1", {"start": v(2.5, 269.17) * mm, "end": v(2.5, 264.17) * mm});
            skLineSegment(sketch, "E4.0.16.2", {"start": v(2.5, 264.17) * mm, "end": v(-2.5, 264.17) * mm});
            skLineSegment(sketch, "E4.0.16.3", {"start": v(-2.5, 269.17) * mm, "end": v(-2.5, 264.17) * mm});
            skLineSegment(sketch, "E4.0.17.0", {"start": v(2.5, 285.83) * mm, "end": v(-2.5, 285.83) * mm});
            skLineSegment(sketch, "E4.0.17.1", {"start": v(2.5, 285.83) * mm, "end": v(2.5, 280.83) * mm});
            skLineSegment(sketch, "E4.0.17.2", {"start": v(2.5, 280.83) * mm, "end": v(-2.5, 280.83) * mm});
            skLineSegment(sketch, "E4.0.17.3", {"start": v(-2.5, 285.83) * mm, "end": v(-2.5, 280.83) * mm});
            skLineSegment(sketch, "E4.0.18.0", {"start": v(2.5, 302.5) * mm, "end": v(-2.5, 302.5) * mm});
            skLineSegment(sketch, "E4.0.18.1", {"start": v(2.5, 302.5) * mm, "end": v(2.5, 297.5) * mm});
            skLineSegment(sketch, "E4.0.18.2", {"start": v(2.5, 297.5) * mm, "end": v(-2.5, 297.5) * mm});
            skLineSegment(sketch, "E4.0.18.3", {"start": v(-2.5, 302.5) * mm, "end": v(-2.5, 297.5) * mm});
            skLineSegment(sketch, "E4.0.19.0", {"start": v(2.5, 319.17) * mm, "end": v(-2.5, 319.17) * mm});
            skLineSegment(sketch, "E4.0.19.1", {"start": v(2.5, 319.17) * mm, "end": v(2.5, 314.17) * mm});
            skLineSegment(sketch, "E4.0.19.2", {"start": v(2.5, 314.17) * mm, "end": v(-2.5, 314.17) * mm});
            skLineSegment(sketch, "E4.0.19.3", {"start": v(-2.5, 319.17) * mm, "end": v(-2.5, 314.17) * mm});
            skLineSegment(sketch, "E4.0.20.0", {"start": v(2.5, 335.83) * mm, "end": v(-2.5, 335.83) * mm});
            skLineSegment(sketch, "E4.0.20.1", {"start": v(2.5, 335.83) * mm, "end": v(2.5, 330.83) * mm});
            skLineSegment(sketch, "E4.0.20.2", {"start": v(2.5, 330.83) * mm, "end": v(-2.5, 330.83) * mm});
            skLineSegment(sketch, "E4.0.20.3", {"start": v(-2.5, 335.83) * mm, "end": v(-2.5, 330.83) * mm});
            skLineSegment(sketch, "E4.0.21.0", {"start": v(2.5, 352.5) * mm, "end": v(-2.5, 352.5) * mm});
            skLineSegment(sketch, "E4.0.21.1", {"start": v(2.5, 352.5) * mm, "end": v(2.5, 347.5) * mm});
            skLineSegment(sketch, "E4.0.21.2", {"start": v(2.5, 347.5) * mm, "end": v(-2.5, 347.5) * mm});
            skLineSegment(sketch, "E4.0.21.3", {"start": v(-2.5, 352.5) * mm, "end": v(-2.5, 347.5) * mm});
            skLineSegment(sketch, "E4.0.22.0", {"start": v(2.5, 369.17) * mm, "end": v(-2.5, 369.17) * mm});
            skLineSegment(sketch, "E4.0.22.1", {"start": v(2.5, 369.17) * mm, "end": v(2.5, 364.17) * mm});
            skLineSegment(sketch, "E4.0.22.2", {"start": v(2.5, 364.17) * mm, "end": v(-2.5, 364.17) * mm});
            skLineSegment(sketch, "E4.0.22.3", {"start": v(-2.5, 369.17) * mm, "end": v(-2.5, 364.17) * mm});
            skLineSegment(sketch, "E4.0.23.0", {"start": v(2.5, 385.83) * mm, "end": v(-2.5, 385.83) * mm});
            skLineSegment(sketch, "E4.0.23.1", {"start": v(2.5, 385.83) * mm, "end": v(2.5, 380.83) * mm});
            skLineSegment(sketch, "E4.0.23.2", {"start": v(2.5, 380.83) * mm, "end": v(-2.5, 380.83) * mm});
            skLineSegment(sketch, "E4.0.23.3", {"start": v(-2.5, 385.83) * mm, "end": v(-2.5, 380.83) * mm});
            skLineSegment(sketch, "E4.0.24.0", {"start": v(2.5, 402.5) * mm, "end": v(-2.5, 402.5) * mm});
            skLineSegment(sketch, "E4.0.24.1", {"start": v(2.5, 402.5) * mm, "end": v(2.5, 397.5) * mm});
            skLineSegment(sketch, "E4.0.24.2", {"start": v(2.5, 397.5) * mm, "end": v(-2.5, 397.5) * mm});
            skLineSegment(sketch, "E4.0.24.3", {"start": v(-2.5, 402.5) * mm, "end": v(-2.5, 397.5) * mm});
            skLineSegment(sketch, "E4.0.25.0", {"start": v(2.5, 419.17) * mm, "end": v(-2.5, 419.17) * mm});
            skLineSegment(sketch, "E4.0.25.1", {"start": v(2.5, 419.17) * mm, "end": v(2.5, 414.17) * mm});
            skLineSegment(sketch, "E4.0.25.2", {"start": v(2.5, 414.17) * mm, "end": v(-2.5, 414.17) * mm});
            skLineSegment(sketch, "E4.0.25.3", {"start": v(-2.5, 419.17) * mm, "end": v(-2.5, 414.17) * mm});
            skLineSegment(sketch, "E4.0.26.0", {"start": v(2.5, 435.83) * mm, "end": v(-2.5, 435.83) * mm});
            skLineSegment(sketch, "E4.0.26.1", {"start": v(2.5, 435.83) * mm, "end": v(2.5, 430.83) * mm});
            skLineSegment(sketch, "E4.0.26.2", {"start": v(2.5, 430.83) * mm, "end": v(-2.5, 430.83) * mm});
            skLineSegment(sketch, "E4.0.26.3", {"start": v(-2.5, 435.83) * mm, "end": v(-2.5, 430.83) * mm});
            skLineSegment(sketch, "E4.0.27.0", {"start": v(2.5, 452.5) * mm, "end": v(-2.5, 452.5) * mm});
            skLineSegment(sketch, "E4.0.27.1", {"start": v(2.5, 452.5) * mm, "end": v(2.5, 447.5) * mm});
            skLineSegment(sketch, "E4.0.27.2", {"start": v(2.5, 447.5) * mm, "end": v(-2.5, 447.5) * mm});
            skLineSegment(sketch, "E4.0.27.3", {"start": v(-2.5, 452.5) * mm, "end": v(-2.5, 447.5) * mm});
            skLineSegment(sketch, "E4.0.28.0", {"start": v(2.5, 469.17) * mm, "end": v(-2.5, 469.17) * mm});
            skLineSegment(sketch, "E4.0.28.1", {"start": v(2.5, 469.17) * mm, "end": v(2.5, 464.17) * mm});
            skLineSegment(sketch, "E4.0.28.2", {"start": v(2.5, 464.17) * mm, "end": v(-2.5, 464.17) * mm});
            skLineSegment(sketch, "E4.0.28.3", {"start": v(-2.5, 469.17) * mm, "end": v(-2.5, 464.17) * mm});
            skLineSegment(sketch, "E4.0.29.0", {"start": v(2.5, 485.83) * mm, "end": v(-2.5, 485.83) * mm});
            skLineSegment(sketch, "E4.0.29.1", {"start": v(2.5, 485.83) * mm, "end": v(2.5, 480.83) * mm});
            skLineSegment(sketch, "E4.0.29.2", {"start": v(2.5, 480.83) * mm, "end": v(-2.5, 480.83) * mm});
            skLineSegment(sketch, "E4.0.29.3", {"start": v(-2.5, 485.83) * mm, "end": v(-2.5, 480.83) * mm});
            skLineSegment(sketch, "E4.0.30.0", {"start": v(2.5, 502.5) * mm, "end": v(-2.5, 502.5) * mm});
            skLineSegment(sketch, "E4.0.30.1", {"start": v(2.5, 502.5) * mm, "end": v(2.5, 497.5) * mm});
            skLineSegment(sketch, "E4.0.30.2", {"start": v(2.5, 497.5) * mm, "end": v(-2.5, 497.5) * mm});
            skLineSegment(sketch, "E4.0.30.3", {"start": v(-2.5, 502.5) * mm, "end": v(-2.5, 497.5) * mm});
            skLineSegment(sketch, "E4.0.31.0", {"start": v(2.5, 519.17) * mm, "end": v(-2.5, 519.17) * mm});
            skLineSegment(sketch, "E4.0.31.1", {"start": v(2.5, 519.17) * mm, "end": v(2.5, 514.17) * mm});
            skLineSegment(sketch, "E4.0.31.2", {"start": v(2.5, 514.17) * mm, "end": v(-2.5, 514.17) * mm});
            skLineSegment(sketch, "E4.0.31.3", {"start": v(-2.5, 519.17) * mm, "end": v(-2.5, 514.17) * mm});
            skLineSegment(sketch, "E4.0.32.0", {"start": v(2.5, 535.83) * mm, "end": v(-2.5, 535.83) * mm});
            skLineSegment(sketch, "E4.0.32.1", {"start": v(2.5, 535.83) * mm, "end": v(2.5, 530.83) * mm});
            skLineSegment(sketch, "E4.0.32.2", {"start": v(2.5, 530.83) * mm, "end": v(-2.5, 530.83) * mm});
            skLineSegment(sketch, "E4.0.32.3", {"start": v(-2.5, 535.83) * mm, "end": v(-2.5, 530.83) * mm});
            skLineSegment(sketch, "E4.0.33.0", {"start": v(2.5, 552.5) * mm, "end": v(-2.5, 552.5) * mm});
            skLineSegment(sketch, "E4.0.33.1", {"start": v(2.5, 552.5) * mm, "end": v(2.5, 547.5) * mm});
            skLineSegment(sketch, "E4.0.33.2", {"start": v(2.5, 547.5) * mm, "end": v(-2.5, 547.5) * mm});
            skLineSegment(sketch, "E4.0.33.3", {"start": v(-2.5, 552.5) * mm, "end": v(-2.5, 547.5) * mm});
            skLineSegment(sketch, "E4.0.34.0", {"start": v(2.5, 569.17) * mm, "end": v(-2.5, 569.17) * mm});
            skLineSegment(sketch, "E4.0.34.1", {"start": v(2.5, 569.17) * mm, "end": v(2.5, 564.17) * mm});
            skLineSegment(sketch, "E4.0.34.2", {"start": v(2.5, 564.17) * mm, "end": v(-2.5, 564.17) * mm});
            skLineSegment(sketch, "E4.0.34.3", {"start": v(-2.5, 569.17) * mm, "end": v(-2.5, 564.17) * mm});
            skLineSegment(sketch, "E4.0.35.0", {"start": v(2.5, 585.83) * mm, "end": v(-2.5, 585.83) * mm});
            skLineSegment(sketch, "E4.0.35.1", {"start": v(2.5, 585.83) * mm, "end": v(2.5, 580.83) * mm});
            skLineSegment(sketch, "E4.0.35.2", {"start": v(2.5, 580.83) * mm, "end": v(-2.5, 580.83) * mm});
            skLineSegment(sketch, "E4.0.35.3", {"start": v(-2.5, 585.83) * mm, "end": v(-2.5, 580.83) * mm});
            skLineSegment(sketch, "E4.0.36.0", {"start": v(2.5, 602.5) * mm, "end": v(-2.5, 602.5) * mm});
            skLineSegment(sketch, "E4.0.36.1", {"start": v(2.5, 602.5) * mm, "end": v(2.5, 597.5) * mm});
            skLineSegment(sketch, "E4.0.36.2", {"start": v(2.5, 597.5) * mm, "end": v(-2.5, 597.5) * mm});
            skLineSegment(sketch, "E4.0.36.3", {"start": v(-2.5, 602.5) * mm, "end": v(-2.5, 597.5) * mm});
            skLineSegment(sketch, "E4.0.37.0", {"start": v(2.5, 619.17) * mm, "end": v(-2.5, 619.17) * mm});
            skLineSegment(sketch, "E4.0.37.1", {"start": v(2.5, 619.17) * mm, "end": v(2.5, 614.17) * mm});
            skLineSegment(sketch, "E4.0.37.2", {"start": v(2.5, 614.17) * mm, "end": v(-2.5, 614.17) * mm});
            skLineSegment(sketch, "E4.0.37.3", {"start": v(-2.5, 619.17) * mm, "end": v(-2.5, 614.17) * mm});
            skLineSegment(sketch, "E4.0.38.0", {"start": v(2.5, 635.83) * mm, "end": v(-2.5, 635.83) * mm});
            skLineSegment(sketch, "E4.0.38.1", {"start": v(2.5, 635.83) * mm, "end": v(2.5, 630.83) * mm});
            skLineSegment(sketch, "E4.0.38.2", {"start": v(2.5, 630.83) * mm, "end": v(-2.5, 630.83) * mm});
            skLineSegment(sketch, "E4.0.38.3", {"start": v(-2.5, 635.83) * mm, "end": v(-2.5, 630.83) * mm});
            skLineSegment(sketch, "E4.0.39.0", {"start": v(2.5, 652.5) * mm, "end": v(-2.5, 652.5) * mm});
            skLineSegment(sketch, "E4.0.39.1", {"start": v(2.5, 652.5) * mm, "end": v(2.5, 647.5) * mm});
            skLineSegment(sketch, "E4.0.39.2", {"start": v(2.5, 647.5) * mm, "end": v(-2.5, 647.5) * mm});
            skLineSegment(sketch, "E4.0.39.3", {"start": v(-2.5, 652.5) * mm, "end": v(-2.5, 647.5) * mm});
            skLineSegment(sketch, "E4.0.40.0", {"start": v(2.5, 669.17) * mm, "end": v(-2.5, 669.17) * mm});
            skLineSegment(sketch, "E4.0.40.1", {"start": v(2.5, 669.17) * mm, "end": v(2.5, 664.17) * mm});
            skLineSegment(sketch, "E4.0.40.2", {"start": v(2.5, 664.17) * mm, "end": v(-2.5, 664.17) * mm});
            skLineSegment(sketch, "E4.0.40.3", {"start": v(-2.5, 669.17) * mm, "end": v(-2.5, 664.17) * mm});
            skLineSegment(sketch, "E4.0.41.0", {"start": v(2.5, 685.83) * mm, "end": v(-2.5, 685.83) * mm});
            skLineSegment(sketch, "E4.0.41.1", {"start": v(2.5, 685.83) * mm, "end": v(2.5, 680.83) * mm});
            skLineSegment(sketch, "E4.0.41.2", {"start": v(2.5, 680.83) * mm, "end": v(-2.5, 680.83) * mm});
            skLineSegment(sketch, "E4.0.41.3", {"start": v(-2.5, 685.83) * mm, "end": v(-2.5, 680.83) * mm});
            skLineSegment(sketch, "E4.0.42.0", {"start": v(2.5, 702.5) * mm, "end": v(-2.5, 702.5) * mm});
            skLineSegment(sketch, "E4.0.42.1", {"start": v(2.5, 702.5) * mm, "end": v(2.5, 697.5) * mm});
            skLineSegment(sketch, "E4.0.42.2", {"start": v(2.5, 697.5) * mm, "end": v(-2.5, 697.5) * mm});
            skLineSegment(sketch, "E4.0.42.3", {"start": v(-2.5, 702.5) * mm, "end": v(-2.5, 697.5) * mm});
            skLineSegment(sketch, "E4.0.43.0", {"start": v(2.5, 719.17) * mm, "end": v(-2.5, 719.17) * mm});
            skLineSegment(sketch, "E4.0.43.1", {"start": v(2.5, 719.17) * mm, "end": v(2.5, 714.17) * mm});
            skLineSegment(sketch, "E4.0.43.2", {"start": v(2.5, 714.17) * mm, "end": v(-2.5, 714.17) * mm});
            skLineSegment(sketch, "E4.0.43.3", {"start": v(-2.5, 719.17) * mm, "end": v(-2.5, 714.17) * mm});
            skLineSegment(sketch, "E4.0.44.0", {"start": v(2.5, 735.83) * mm, "end": v(-2.5, 735.83) * mm});
            skLineSegment(sketch, "E4.0.44.1", {"start": v(2.5, 735.83) * mm, "end": v(2.5, 730.83) * mm});
            skLineSegment(sketch, "E4.0.44.2", {"start": v(2.5, 730.83) * mm, "end": v(-2.5, 730.83) * mm});
            skLineSegment(sketch, "E4.0.44.3", {"start": v(-2.5, 735.83) * mm, "end": v(-2.5, 730.83) * mm});
            skLineSegment(sketch, "E4.0.45.0", {"start": v(2.5, 752.5) * mm, "end": v(-2.5, 752.5) * mm});
            skLineSegment(sketch, "E4.0.45.1", {"start": v(2.5, 752.5) * mm, "end": v(2.5, 747.5) * mm});
            skLineSegment(sketch, "E4.0.45.2", {"start": v(2.5, 747.5) * mm, "end": v(-2.5, 747.5) * mm});
            skLineSegment(sketch, "E4.0.45.3", {"start": v(-2.5, 752.5) * mm, "end": v(-2.5, 747.5) * mm});
            skLineSegment(sketch, "E4.0.46.0", {"start": v(2.5, 769.17) * mm, "end": v(-2.5, 769.17) * mm});
            skLineSegment(sketch, "E4.0.46.1", {"start": v(2.5, 769.17) * mm, "end": v(2.5, 764.17) * mm});
            skLineSegment(sketch, "E4.0.46.2", {"start": v(2.5, 764.17) * mm, "end": v(-2.5, 764.17) * mm});
            skLineSegment(sketch, "E4.0.46.3", {"start": v(-2.5, 769.17) * mm, "end": v(-2.5, 764.17) * mm});
            skLineSegment(sketch, "E4.0.47.0", {"start": v(2.5, 785.83) * mm, "end": v(-2.5, 785.83) * mm});
            skLineSegment(sketch, "E4.0.47.1", {"start": v(2.5, 785.83) * mm, "end": v(2.5, 780.83) * mm});
            skLineSegment(sketch, "E4.0.47.2", {"start": v(2.5, 780.83) * mm, "end": v(-2.5, 780.83) * mm});
            skLineSegment(sketch, "E4.0.47.3", {"start": v(-2.5, 785.83) * mm, "end": v(-2.5, 780.83) * mm});
            skLineSegment(sketch, "E4.0.48.0", {"start": v(2.5, 802.5) * mm, "end": v(-2.5, 802.5) * mm});
            skLineSegment(sketch, "E4.0.48.1", {"start": v(2.5, 802.5) * mm, "end": v(2.5, 797.5) * mm});
            skLineSegment(sketch, "E4.0.48.2", {"start": v(2.5, 797.5) * mm, "end": v(-2.5, 797.5) * mm});
            skLineSegment(sketch, "E4.0.48.3", {"start": v(-2.5, 802.5) * mm, "end": v(-2.5, 797.5) * mm});
            skLineSegment(sketch, "E4.0.49.0", {"start": v(2.5, 819.17) * mm, "end": v(-2.5, 819.17) * mm});
            skLineSegment(sketch, "E4.0.49.1", {"start": v(2.5, 819.17) * mm, "end": v(2.5, 814.17) * mm});
            skLineSegment(sketch, "E4.0.49.2", {"start": v(2.5, 814.17) * mm, "end": v(-2.5, 814.17) * mm});
            skLineSegment(sketch, "E4.0.49.3", {"start": v(-2.5, 819.17) * mm, "end": v(-2.5, 814.17) * mm});
            skLineSegment(sketch, "E4.0.50.0", {"start": v(2.5, 835.83) * mm, "end": v(-2.5, 835.83) * mm});
            skLineSegment(sketch, "E4.0.50.1", {"start": v(2.5, 835.83) * mm, "end": v(2.5, 830.83) * mm});
            skLineSegment(sketch, "E4.0.50.2", {"start": v(2.5, 830.83) * mm, "end": v(-2.5, 830.83) * mm});
            skLineSegment(sketch, "E4.0.50.3", {"start": v(-2.5, 835.83) * mm, "end": v(-2.5, 830.83) * mm});
            skLineSegment(sketch, "E4.0.51.0", {"start": v(2.5, 852.5) * mm, "end": v(-2.5, 852.5) * mm});
            skLineSegment(sketch, "E4.0.51.1", {"start": v(2.5, 852.5) * mm, "end": v(2.5, 847.5) * mm});
            skLineSegment(sketch, "E4.0.51.2", {"start": v(2.5, 847.5) * mm, "end": v(-2.5, 847.5) * mm});
            skLineSegment(sketch, "E4.0.51.3", {"start": v(-2.5, 852.5) * mm, "end": v(-2.5, 847.5) * mm});
            skLineSegment(sketch, "E4.0.52.0", {"start": v(2.5, 869.17) * mm, "end": v(-2.5, 869.17) * mm});
            skLineSegment(sketch, "E4.0.52.1", {"start": v(2.5, 869.17) * mm, "end": v(2.5, 864.17) * mm});
            skLineSegment(sketch, "E4.0.52.2", {"start": v(2.5, 864.17) * mm, "end": v(-2.5, 864.17) * mm});
            skLineSegment(sketch, "E4.0.52.3", {"start": v(-2.5, 869.17) * mm, "end": v(-2.5, 864.17) * mm});
            skLineSegment(sketch, "E4.0.53.0", {"start": v(2.5, 885.83) * mm, "end": v(-2.5, 885.83) * mm});
            skLineSegment(sketch, "E4.0.53.1", {"start": v(2.5, 885.83) * mm, "end": v(2.5, 880.83) * mm});
            skLineSegment(sketch, "E4.0.53.2", {"start": v(2.5, 880.83) * mm, "end": v(-2.5, 880.83) * mm});
            skLineSegment(sketch, "E4.0.53.3", {"start": v(-2.5, 885.83) * mm, "end": v(-2.5, 880.83) * mm});
            skLineSegment(sketch, "E4.0.54.0", {"start": v(2.5, 902.5) * mm, "end": v(-2.5, 902.5) * mm});
            skLineSegment(sketch, "E4.0.54.1", {"start": v(2.5, 902.5) * mm, "end": v(2.5, 897.5) * mm});
            skLineSegment(sketch, "E4.0.54.2", {"start": v(2.5, 897.5) * mm, "end": v(-2.5, 897.5) * mm});
            skLineSegment(sketch, "E4.0.54.3", {"start": v(-2.5, 902.5) * mm, "end": v(-2.5, 897.5) * mm});
            skLineSegment(sketch, "E4.0.55.0", {"start": v(2.5, 919.17) * mm, "end": v(-2.5, 919.17) * mm});
            skLineSegment(sketch, "E4.0.55.1", {"start": v(2.5, 919.17) * mm, "end": v(2.5, 914.17) * mm});
            skLineSegment(sketch, "E4.0.55.2", {"start": v(2.5, 914.17) * mm, "end": v(-2.5, 914.17) * mm});
            skLineSegment(sketch, "E4.0.55.3", {"start": v(-2.5, 919.17) * mm, "end": v(-2.5, 914.17) * mm});
            skLineSegment(sketch, "E4.0.56.0", {"start": v(2.5, 935.83) * mm, "end": v(-2.5, 935.83) * mm});
            skLineSegment(sketch, "E4.0.56.1", {"start": v(2.5, 935.83) * mm, "end": v(2.5, 930.83) * mm});
            skLineSegment(sketch, "E4.0.56.2", {"start": v(2.5, 930.83) * mm, "end": v(-2.5, 930.83) * mm});
            skLineSegment(sketch, "E4.0.56.3", {"start": v(-2.5, 935.83) * mm, "end": v(-2.5, 930.83) * mm});
            skLineSegment(sketch, "E4.0.57.0", {"start": v(2.5, 952.5) * mm, "end": v(-2.5, 952.5) * mm});
            skLineSegment(sketch, "E4.0.57.1", {"start": v(2.5, 952.5) * mm, "end": v(2.5, 947.5) * mm});
            skLineSegment(sketch, "E4.0.57.2", {"start": v(2.5, 947.5) * mm, "end": v(-2.5, 947.5) * mm});
            skLineSegment(sketch, "E4.0.57.3", {"start": v(-2.5, 952.5) * mm, "end": v(-2.5, 947.5) * mm});
            skLineSegment(sketch, "E4.0.58.0", {"start": v(2.5, 969.17) * mm, "end": v(-2.5, 969.17) * mm});
            skLineSegment(sketch, "E4.0.58.1", {"start": v(2.5, 969.17) * mm, "end": v(2.5, 964.17) * mm});
            skLineSegment(sketch, "E4.0.58.2", {"start": v(2.5, 964.17) * mm, "end": v(-2.5, 964.17) * mm});
            skLineSegment(sketch, "E4.0.58.3", {"start": v(-2.5, 969.17) * mm, "end": v(-2.5, 964.17) * mm});
            skLineSegment(sketch, "E4.0.59.0", {"start": v(2.5, 985.83) * mm, "end": v(-2.5, 985.83) * mm});
            skLineSegment(sketch, "E4.0.59.1", {"start": v(2.5, 985.83) * mm, "end": v(2.5, 980.83) * mm});
            skLineSegment(sketch, "E4.0.59.2", {"start": v(2.5, 980.83) * mm, "end": v(-2.5, 980.83) * mm});
            skLineSegment(sketch, "E4.0.59.3", {"start": v(-2.5, 985.83) * mm, "end": v(-2.5, 980.83) * mm});
            skLineSegment(sketch, "E4.direction1", {"start": v(-2.5, 2.5) * mm, "end": v(22.5, 2.5) * mm, "construction": true});
            skLineSegment(sketch, "E4.direction2", {"start": v(-2.5, 2.5) * mm, "end": v(-2.5, 19.17) * mm, "construction": true});
            skSolve(sketch);
        }
        {
            var Q0;
            Q0 = qSketchRegion(id + "F2", true);
            extrude(context, id + "F4", {"entities" : qUnion([Q0]), "operationType" : NewBodyOperationType.ADD, "endBound" : BoundingType.SYMMETRIC, "depth" : 26 * mm, "offsetDistance" : 25 * mm});
        }
        {
            var Q0;
            Q0 = qSketchRegion(id + "F3", true);
            extrude(context, id + "F5", {"entities" : qUnion([Q0]), "operationType" : NewBodyOperationType.ADD, "endBound" : BoundingType.SYMMETRIC, "depth" : 26 * mm, "offsetDistance" : 25 * mm});
        }
    });
